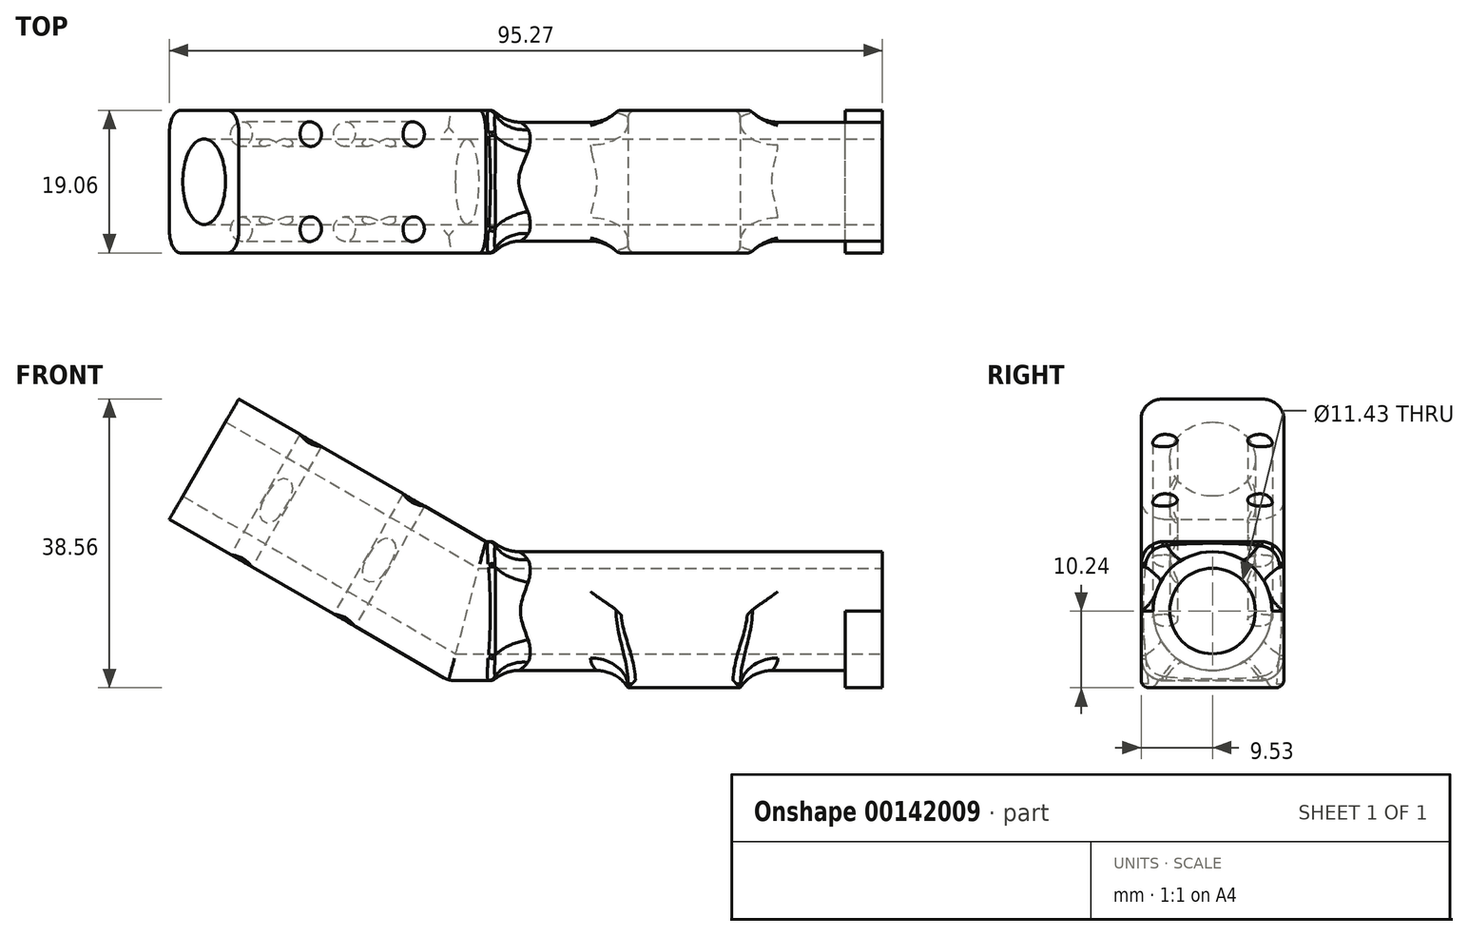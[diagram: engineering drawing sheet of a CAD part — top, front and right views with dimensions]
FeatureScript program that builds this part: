
annotation { "Feature Type Name" : "Feature", "Feature Type Description" : "" }
export const myFeature = defineFeature(function(context is Context, id is Id, definition is map)
    precondition{}
    {
        {
            var Q0;
            Q0=qCreatedBy(makeId("Front.planeOp"),FACE);
            var sketch = newSketch(context, id + "F0", { "sketchPlane" : qUnion([Q0])});
            skLineSegment(sketch, "E0.bottom", {"start": v(4.97, 9.27) * mm, "end": v(57.97, 9.27) * mm});
            skLineSegment(sketch, "E0.top", {"start": v(0, -9.27) * mm, "end": v(57.97, -9.27) * mm});
            skLineSegment(sketch, "E0.right", {"start": v(57.97, 9.27) * mm, "end": v(57.97, -9.27) * mm});
            skLineSegment(sketch, "E1", {"start": v(0, 0) * mm, "end": v(57.97, 0) * mm, "construction": true});
            skLineSegment(sketch, "E2", {"start": v(4.97, 9.27) * mm, "end": v(-28.03, 28.32) * mm});
            skLineSegment(sketch, "E3", {"start": v(-37.3, 12.26) * mm, "end": v(-28.03, 28.32) * mm});
            skPoint(sketch, "E4.orphan", {"position": v(0, 13.5) * mm});
            skLineSegment(sketch, "E5", {"start": v(-37.3, 12.26) * mm, "end": v(0, -9.27) * mm});
            skSolve(sketch);
        }
        {
            var Q0;
            Q0=qSketchRegion(id+"F0",true);
            extrude(context, id + "F1", {"entities" : qUnion([Q0]), "depth" : 9.52 * mm, "hasSecondDirection" : true, "secondDirectionOppositeDirection" : true, "secondDirectionDepth" : 9.52 * mm});
        }
        {
            var Q0;
            Q0=makeQuery(id+"F1.opExtrude","SWEPT_FACE",FACE,{"disambiguationData":[OSD([sQuery(id+"F0.wireOp",EDGE,"E5")])]});
            var sketch = newSketch(context, id + "F2", { "sketchPlane" : qUnion([Q0])});
            skLineSegment(sketch, "E6.bottom", {"start": v(-38.43, -9.53) * mm, "end": v(-0.33, -9.53) * mm});
            skLineSegment(sketch, "E6.top", {"start": v(-38.43, 9.53) * mm, "end": v(-0.33, 9.53) * mm});
            skLineSegment(sketch, "E6.left", {"start": v(-38.43, -9.53) * mm, "end": v(-38.43, 9.53) * mm});
            skLineSegment(sketch, "E6.right", {"start": v(-0.33, -9.52) * mm, "end": v(-0.33, 9.53) * mm});
            skLineSegment(sketch, "E7", {"start": v(-38.43, 0) * mm, "end": v(-0.33, 0) * mm, "construction": true});
            skLineSegment(sketch, "E8", {"start": v(-19.38, 9.53) * mm, "end": v(-19.38, -9.53) * mm, "construction": true});
            skLineSegment(sketch, "E9.bottom", {"start": v(-27.32, -6.35) * mm, "end": v(-11.45, -6.35) * mm, "construction": true});
            skLineSegment(sketch, "E9.top", {"start": v(-27.32, 6.35) * mm, "end": v(-11.45, 6.35) * mm, "construction": true});
            skLineSegment(sketch, "E9.left", {"start": v(-27.32, -6.35) * mm, "end": v(-27.32, 6.35) * mm, "construction": true});
            skLineSegment(sketch, "E9.right", {"start": v(-11.45, -6.35) * mm, "end": v(-11.45, 6.35) * mm, "construction": true});
            skPoint(sketch, "E9.middle", {"position": v(-19.38, 0) * mm});
            skSolve(sketch);
        }
        {
            var Q0;
            Q0=sQuery(id+"F2.wireOp",VERTEX,"E9.left.end");
            var Q1;
            Q1=sQuery(id+"F2.wireOp",VERTEX,"E9.left.start");
            var Q2;
            Q2=sQuery(id+"F2.wireOp",VERTEX,"E9.right.start");
            var Q3;
            Q3=sQuery(id+"F2.wireOp",VERTEX,"E9.top.end");
            var Q4;
            Q4=makeQuery(id+"F1.opExtrude","SWEPT_BODY",BODY,{"disambiguationData":[OSD([sQuery(id+"F0.wireOp",EDGE,"E0.bottom"),sQuery(id+"F0.wireOp",EDGE,"E0.top"),sQuery(id+"F0.wireOp",EDGE,"E0.right"),sQuery(id+"F0.wireOp",EDGE,"E2"),sQuery(id+"F0.wireOp",EDGE,"95kfVAff-3bN3-xnc1-YnyT-jtpb1TC5GENx"),sQuery(id+"F0.wireOp",EDGE,"E3")])]});
            hole(context, id + "F3", {"style" : HoleStyle.SIMPLE, "endStyle" : HoleEndStyle.THROUGH, "standardTappedOrClearance" : lookupTablePath({ "standard" : "ISO", "fit" : "Normal", "size" : "M3", "type" : "Clearance" }), "standardBlindInLast" : lookupTablePath({ "fit" : "Standard", "standard" : "ISO", "size" : "M3", "type" : "Clearance" }), "holeDiameter" : 3.3 * mm, "locations" : qUnion([Q0, Q1, Q2, Q3]), "scope" : qUnion([Q4]), "isTappedThrough" : true});
        }
        {
            var Q0;
            Q0=makeQuery(id+"F1.opExtrude","SWEPT_FACE",FACE,{"disambiguationData":[OSD([sQuery(id+"F0.wireOp",EDGE,"E3")])]});
            var sketch = newSketch(context, id + "F4", { "sketchPlane" : qUnion([Q0])});
            skLineSegment(sketch, "E10", {"start": v(0, 10.51) * mm, "end": v(0, -8.03) * mm, "construction": true});
            skCircle(sketch, "E11", {"center": v(0, 1.24) * mm, "radius": 5.72 * mm});
            skSolve(sketch);
        }
        {
            var Q0;
            Q0=qCreatedBy(makeId("Front.planeOp"),FACE);
            var sketch = newSketch(context, id + "F5", { "sketchPlane" : qUnion([Q0])});
            skLineSegment(sketch, "E12", {"start": v(-32.66, 20.3) * mm, "end": v(2.48, 0) * mm});
            skLineSegment(sketch, "E13", {"start": v(2.48, 0) * mm, "end": v(57.97, 0) * mm});
            skPoint(sketch, "E14", {"position": v(57.97, 0) * mm});
            skSolve(sketch);
        }
        {
            var Q0;
            Q0=qSketchRegion(id+"F4",true);
            var Q1;
            Q1=qConstructionFilter(qBodyType(qCreatedBy(id+"F5",EDGE),BodyType.WIRE),ConstructionObject.NO);
            sweep(context, id + "F6", {"operationType" : NewBodyOperationType.REMOVE, "profiles" : qUnion([Q0]), "path" : qUnion([Q1])});
        }
        {
            var Q0;
            Q0=makeQuery(id+"F1.opExtrude","SWEPT_FACE",FACE,{"disambiguationData":[OSD([sQuery(id+"F0.wireOp",EDGE,"E0.right")])]});
            var sketch = newSketch(context, id + "F7", { "sketchPlane" : qUnion([Q0])});
            skCircle(sketch, "E15", {"center": v(0, 0) * mm, "radius": 7.94 * mm});
            skLineSegment(sketch, "E16.0.0", {"start": v(9.53, -9.27) * mm, "end": v(9.53, 9.27) * mm});
            skLineSegment(sketch, "E16.0.1", {"start": v(9.52, 9.27) * mm, "end": v(-9.53, 9.27) * mm});
            skLineSegment(sketch, "E16.0.2", {"start": v(-9.53, 9.27) * mm, "end": v(-9.53, -9.27) * mm});
            skLineSegment(sketch, "E16.0.3", {"start": v(-9.53, -9.27) * mm, "end": v(9.52, -9.27) * mm});
            skSolve(sketch);
        }
        {
            var Q0;
            Q0=qSketchRegion(id+"F7",true);
            extrude(context, id + "F8", {"entities" : qUnion([Q0]), "operationType" : NewBodyOperationType.REMOVE, "oppositeDirection" : true, "depth" : 52 * mm});
        }
        {
            var Q0;
            Q0=makeQuery(id+"F1.opExtrude","SWEPT_FACE",FACE,{"disambiguationData":[OSD([sQuery(id+"F0.wireOp",EDGE,"E2")])]});
            var sketch = newSketch(context, id + "F9", { "sketchPlane" : qUnion([Q0])});
            skCircle(sketch, "E17.0", {"center": v(-27.32, -6.35) * mm, "radius": 1.65 * mm});
            skCircle(sketch, "E17.1", {"center": v(-27.32, 6.35) * mm, "radius": 1.65 * mm});
            skCircle(sketch, "E17.2", {"center": v(-11.45, -6.35) * mm, "radius": 1.65 * mm});
            skCircle(sketch, "E17.3", {"center": v(-11.45, 6.35) * mm, "radius": 1.65 * mm});
            skCircle(sketch, "E18", {"center": v(-27.32, -6.35) * mm, "radius": 3.18 * mm});
            skCircle(sketch, "E19", {"center": v(-27.32, 6.35) * mm, "radius": 3.18 * mm});
            skCircle(sketch, "E20", {"center": v(-11.45, 6.35) * mm, "radius": 3.18 * mm});
            skCircle(sketch, "E21", {"center": v(-11.45, -6.35) * mm, "radius": 3.18 * mm});
            skSolve(sketch);
        }
        {
            var Q0;
            Q0=makeQuery(id+"F1.opExtrude","CAP_EDGE",EDGE,{"disambiguationData":[OSD([sQuery(id+"F0.wireOp",EDGE,"E2")])],"isStart":true});
            var Q1;
            Q1=makeQuery(id+"F1.opExtrude","CAP_EDGE",EDGE,{"disambiguationData":[OSD([sQuery(id+"F0.wireOp",EDGE,"E2")])],"isStart":false});
            var Q2;
            Q2=makeQuery(id+"F1.opExtrude","CAP_EDGE",EDGE,{"disambiguationData":[OSD([sQuery(id+"F0.wireOp",EDGE,"E5")])],"isStart":false});
            var Q3;
            Q3=makeQuery(id+"F1.opExtrude","CAP_EDGE",EDGE,{"disambiguationData":[OSD([sQuery(id+"F0.wireOp",EDGE,"E5")])],"isStart":true});
            var Q4;
            Q4=makeQuery(id+"F1.opExtrude","CAP_EDGE",EDGE,{"disambiguationData":[OSD([sQuery(id+"F0.wireOp",EDGE,"E0.top")])],"isStart":false});
            var Q5;
            Q5=makeQuery(id+"F1.opExtrude","CAP_EDGE",EDGE,{"disambiguationData":[OSD([sQuery(id+"F0.wireOp",EDGE,"E0.top")])],"isStart":true});
            var Q6;
            {var subQ0=sQuery(id+"F0.wireOp",EDGE,"E2");var subQ1=sQuery(id+"F0.wireOp",EDGE,"E0.bottom");Q6=makeQuery(id+"FvCCCtX8j9DAQVm_1.opFillet","BLEND_EDGE",EDGE,{"blendedFrom":[makeQuery(id+"F1.opExtrude","SWEPT_EDGE",EDGE,{"disambiguationData":[OSD([subQ1,subQ0])]}),makeQuery(id+"F1.opExtrude","CAP_FACE",FACE,{"disambiguationData":[OSD([subQ1,sQuery(id+"F0.wireOp",EDGE,"E0.top"),sQuery(id+"F0.wireOp",EDGE,"E0.right"),subQ0,sQuery(id+"F0.wireOp",EDGE,"E3"),sQuery(id+"F0.wireOp",EDGE,"E5")])],"isStart":false})],"blendedInto":[makeQuery(id+"F1.opExtrude","CAP_FACE",FACE,{"disambiguationData":[OSD([subQ1,sQuery(id+"F0.wireOp",EDGE,"E0.top"),sQuery(id+"F0.wireOp",EDGE,"E0.right"),subQ0,sQuery(id+"F0.wireOp",EDGE,"E3"),sQuery(id+"F0.wireOp",EDGE,"E5")])],"isStart":false})]});}
            var Q7;
            Q7=makeQuery(id+"F1.opExtrude","CAP_EDGE",EDGE,{"disambiguationData":[OSD([sQuery(id+"F0.wireOp",EDGE,"E0.bottom")])],"isStart":false});
            var Q8;
            {var subQ0=sQuery(id+"F0.wireOp",EDGE,"E2");var subQ1=sQuery(id+"F0.wireOp",EDGE,"E0.bottom");Q8=makeQuery(id+"FvCCCtX8j9DAQVm_1.opFillet","BLEND_EDGE",EDGE,{"blendedFrom":[makeQuery(id+"F1.opExtrude","SWEPT_EDGE",EDGE,{"disambiguationData":[OSD([subQ1,subQ0])]}),makeQuery(id+"F1.opExtrude","CAP_FACE",FACE,{"disambiguationData":[OSD([subQ1,sQuery(id+"F0.wireOp",EDGE,"E0.top"),sQuery(id+"F0.wireOp",EDGE,"E0.right"),subQ0,sQuery(id+"F0.wireOp",EDGE,"E3"),sQuery(id+"F0.wireOp",EDGE,"E5")])],"isStart":true})],"blendedInto":[makeQuery(id+"F1.opExtrude","CAP_FACE",FACE,{"disambiguationData":[OSD([subQ1,sQuery(id+"F0.wireOp",EDGE,"E0.top"),sQuery(id+"F0.wireOp",EDGE,"E0.right"),subQ0,sQuery(id+"F0.wireOp",EDGE,"E3"),sQuery(id+"F0.wireOp",EDGE,"E5")])],"isStart":true})]});}
            var Q9;
            Q9=makeQuery(id+"F1.opExtrude","CAP_EDGE",EDGE,{"disambiguationData":[OSD([sQuery(id+"F0.wireOp",EDGE,"E0.bottom")])],"isStart":true});
            fillet(context, id + "F10", {"entities" : qUnion([Q0, Q1, Q2, Q3, Q4, Q5, Q6, Q7, Q8, Q9]), "radius" : 3 * mm, "allowEdgeOverflow" : false});
        }
        {
            var Q0;
            Q0=qCreatedBy(makeId("Front.planeOp"),FACE);
            var sketch = newSketch(context, id + "F11", { "sketchPlane" : qUnion([Q0])});
            skCircle(sketch, "E22", {"center": v(42.1, 0) * mm, "radius": 1.65 * mm});
            skSolve(sketch);
        }
        {
            var Q0;
            Q0=makeQuery(id+"F1.opExtrude","SWEPT_EDGE",EDGE,{"disambiguationData":[OSD([sQuery(id+"F0.wireOp",EDGE,"E0.top"),sQuery(id+"F0.wireOp",EDGE,"E5")])]});
            var Q1;
            Q1=makeQuery(id+"FvCCCtX8j9DAQVm_1.opFillet","BLEND_EDGE",EDGE,{"blendedFrom":[makeQuery(id+"F8.boolean.opBoolean","COPY",EDGE,{"derivedFrom":makeQuery(id+"F8.opExtrude","CAP_EDGE",EDGE,{"disambiguationData":[OSD([sQuery(id+"F7.wireOp",EDGE,"E15")])],"isStart":false})}),makeQuery(id+"F1.opExtrude","SWEPT_FACE",FACE,{"disambiguationData":[OSD([sQuery(id+"F0.wireOp",EDGE,"E0.top")])]})],"blendedInto":[makeQuery(id+"F1.opExtrude","SWEPT_FACE",FACE,{"disambiguationData":[OSD([sQuery(id+"F0.wireOp",EDGE,"E0.top")])]})]});
            fillet(context, id + "F12", {"entities" : qUnion([Q0, Q1]), "radius" : 2.54 * mm, "allowEdgeOverflow" : false});
        }
        {
            var Q0;
            Q0=qCreatedBy(makeId("Right.planeOp"),FACE);
            var Q1;
            Q1=makeQuery(id+"F1.opExtrude","SWEPT_FACE",FACE,{"disambiguationData":[OSD([sQuery(id+"F0.wireOp",EDGE,"E0.right")])]});
            cPlane(context, id + "F13", {"entities" : qUnion([Q0, Q1]), "cplaneType" : CPlaneType.MID_PLANE, "offset" : 25 * mm, "width" : 150 * mm, "height" : 150 * mm});
        }
        {
            var Q0;
            Q0=qCreatedBy(id+"F13.planeOp",FACE);
            var sketch = newSketch(context, id + "F14", { "sketchPlane" : qUnion([Q0])});
            skCircle(sketch, "E23", {"center": v(0, 0) * mm, "radius": 7.94 * mm, "construction": true});
            skArc(sketch, "E24", {"start": v(-5.72, 0) * mm, "mid": v(0, -5.72) * mm, "end": v(5.72, 0) * mm});
            skLineSegment(sketch, "E25.top", {"start": v(9.53, -10.24) * mm, "end": v(-9.53, -10.24) * mm});
            skLineSegment(sketch, "E25.left", {"start": v(9.53, 0) * mm, "end": v(9.53, -10.24) * mm});
            skLineSegment(sketch, "E25.right", {"start": v(-9.53, 0) * mm, "end": v(-9.53, -10.24) * mm});
            skLineSegment(sketch, "E26", {"start": v(-9.53, 0) * mm, "end": v(-5.72, 0) * mm});
            skLineSegment(sketch, "E27", {"start": v(5.72, 0) * mm, "end": v(9.53, 0) * mm});
            skPoint(sketch, "E25.bottom.end.orphan", {"position": v(-9.53, 10.24) * mm});
            skPoint(sketch, "E28.orphan", {"position": v(9.53, 10.24) * mm});
            skSolve(sketch);
        }
        {
            var Q0;
            Q0 = qSketchRegion(id + "F14", true);
            extrude(context, id + "F15", {"entities" : qUnion([Q0]), "operationType" : NewBodyOperationType.ADD, "depth" : 10 * mm, "hasSecondDirection" : true, "secondDirectionOppositeDirection" : true, "secondDirectionDepth" : 5 * mm});
        }
        {
            var Q0;
            Q0=makeQuery(id+"F8.boolean.opBoolean","COPY",FACE,{"derivedFrom":makeQuery(id+"F8.opExtrude","CAP_FACE",FACE,{"disambiguationData":[OSD([sQuery(id+"F7.wireOp",EDGE,"E15"),sQuery(id+"F7.wireOp",EDGE,"E16.0.0"),sQuery(id+"F7.wireOp",EDGE,"E16.0.1"),sQuery(id+"F7.wireOp",EDGE,"E16.0.2"),sQuery(id+"F7.wireOp",EDGE,"E16.0.3")])],"isStart":false})});
            var sketch = newSketch(context, id + "F16", { "sketchPlane" : qUnion([Q0])});
            skArc(sketch, "E29", {"start": v(7.94, 0) * mm, "mid": v(0, 7.94) * mm, "end": v(-7.94, 0) * mm});
            skPoint(sketch, "E30.firstSnap0", {"position": v(-8.65, 9.27) * mm});
            skLineSegment(sketch, "E30.bottom", {"start": v(-9.53, 9.27) * mm, "end": v(9.53, 9.27) * mm});
            skLineSegment(sketch, "E30.top", {"start": v(-9.52, 0) * mm, "end": v(-7.94, 0) * mm});
            skLineSegment(sketch, "E30.left", {"start": v(-9.53, 9.27) * mm, "end": v(-9.53, 0) * mm});
            skLineSegment(sketch, "E30.right", {"start": v(9.53, 9.27) * mm, "end": v(9.53, 0) * mm});
            skLineSegment(sketch, "E31.trimOffspring", {"start": v(7.94, 0) * mm, "end": v(9.53, 0) * mm});
            skSolve(sketch);
        }
        {
            var Q0;
            Q0=makeQuery(id+"F1.opExtrude","SWEPT_FACE",FACE,{"disambiguationData":[OSD([sQuery(id+"F0.wireOp",EDGE,"E0.right")])]});
            var sketch = newSketch(context, id + "F17", { "sketchPlane" : qUnion([Q0])});
            skArc(sketch, "E32", {"start": v(-7.94, 0) * mm, "mid": v(0, -7.94) * mm, "end": v(7.94, 0) * mm});
            skLineSegment(sketch, "E33.bottom", {"start": v(-9.53, -10.24) * mm, "end": v(9.53, -10.24) * mm});
            skLineSegment(sketch, "E33.top", {"start": v(-9.53, 0) * mm, "end": v(-7.94, 0) * mm});
            skLineSegment(sketch, "E33.left", {"start": v(-9.53, -10.24) * mm, "end": v(-9.53, 0) * mm});
            skLineSegment(sketch, "E33.right", {"start": v(9.53, -10.24) * mm, "end": v(9.52, 0) * mm});
            skLineSegment(sketch, "E34.trimOffspring", {"start": v(7.94, 0) * mm, "end": v(9.52, 0) * mm});
            skSolve(sketch);
        }
        {
            var Q0;
            Q0 = qSketchRegion(id + "F17", true);
            extrude(context, id + "F18", {"entities" : qUnion([Q0]), "operationType" : NewBodyOperationType.ADD, "oppositeDirection" : true, "depth" : 5 * mm});
        }
        {
            var Q0;
            Q0=makeQuery(id+"F8.boolean.opBoolean","COPY",EDGE,{"derivedFrom":makeQuery(id+"F8.opExtrude","CAP_EDGE",EDGE,{"disambiguationData":[OSD([sQuery(id+"F7.wireOp",EDGE,"E15")])],"isStart":false})});
            var Q1;
            Q1=makeQuery(id+"F15.boolean.opBoolean","INTERSECT",EDGE,{"derivedFrom":[makeQuery(id+"F8.boolean.opBoolean","COPY",FACE,{"derivedFrom":makeQuery(id+"F8.opExtrude","SWEPT_FACE",FACE,{"disambiguationData":[OSD([sQuery(id+"F7.wireOp",EDGE,"E15")])]})}),makeQuery(id+"F15.opExtrude","CAP_FACE",FACE,{"disambiguationData":[OSD([sQuery(id+"F14.wireOp",EDGE,"E24"),sQuery(id+"F14.wireOp",EDGE,"E25.top"),sQuery(id+"F14.wireOp",EDGE,"E25.left"),sQuery(id+"F14.wireOp",EDGE,"E25.right"),sQuery(id+"F14.wireOp",EDGE,"E26"),sQuery(id+"F14.wireOp",EDGE,"E27")])],"isStart":false})]});
            var Q2;
            Q2=makeQuery(id+"F15.boolean.opBoolean","INTERSECT",EDGE,{"derivedFrom":[makeQuery(id+"F8.boolean.opBoolean","COPY",FACE,{"derivedFrom":makeQuery(id+"F8.opExtrude","SWEPT_FACE",FACE,{"disambiguationData":[OSD([sQuery(id+"F7.wireOp",EDGE,"E15")])]})}),makeQuery(id+"F15.opExtrude","CAP_FACE",FACE,{"disambiguationData":[OSD([sQuery(id+"F14.wireOp",EDGE,"E24"),sQuery(id+"F14.wireOp",EDGE,"E25.top"),sQuery(id+"F14.wireOp",EDGE,"E25.left"),sQuery(id+"F14.wireOp",EDGE,"E25.right"),sQuery(id+"F14.wireOp",EDGE,"E26"),sQuery(id+"F14.wireOp",EDGE,"E27")])],"isStart":true})]});
            var Q3;
            Q3=makeQuery(id+"F15.boolean.opBoolean","INTERSECT",EDGE,{"derivedFrom":[makeQuery(id+"F8.boolean.opBoolean","COPY",FACE,{"derivedFrom":makeQuery(id+"F8.opExtrude","SWEPT_FACE",FACE,{"disambiguationData":[OSD([sQuery(id+"F7.wireOp",EDGE,"E15")])]})}),makeQuery(id+"F15.opExtrude","SWEPT_FACE",FACE,{"disambiguationData":[OSD([sQuery(id+"F14.wireOp",EDGE,"E26")])]})]});
            var Q4;
            Q4=makeQuery(id+"F15.boolean.opBoolean","INTERSECT",EDGE,{"derivedFrom":[makeQuery(id+"F8.boolean.opBoolean","COPY",FACE,{"derivedFrom":makeQuery(id+"F8.opExtrude","SWEPT_FACE",FACE,{"disambiguationData":[OSD([sQuery(id+"F7.wireOp",EDGE,"E15")])]})}),makeQuery(id+"F15.opExtrude","SWEPT_FACE",FACE,{"disambiguationData":[OSD([sQuery(id+"F14.wireOp",EDGE,"E27")])]})]});
            var Q5;
            Q5=makeQuery(id+"F18.opExtrude","SWEPT_EDGE",EDGE,{"disambiguationData":[OSD([sQuery(id+"F7.wireOp",EDGE,"E15"),sQuery(id+"F17.wireOp",EDGE,"E32"),sQuery(id+"F17.wireOp",EDGE,"E34.trimOffspring")])]});
            var Q6;
            Q6=makeQuery(id+"F18.opExtrude","SWEPT_EDGE",EDGE,{"disambiguationData":[OSD([sQuery(id+"F7.wireOp",EDGE,"E15"),sQuery(id+"F17.wireOp",EDGE,"E32"),sQuery(id+"F17.wireOp",EDGE,"E33.top")])]});
            var Q7;
            Q7=makeQuery(id+"F18.opExtrude","CAP_EDGE",EDGE,{"disambiguationData":[OSD([sQuery(id+"F17.wireOp",EDGE,"E32")])],"isStart":false});
            fillet(context, id + "F19", {"entities" : qUnion([Q0, Q1, Q2, Q3, Q4, Q5, Q6, Q7]), "radius" : 5 * mm, "tangentPropagation" : true, "allowEdgeOverflow" : false});
        }
        {
            var Q0;
            Q0=makeQuery(id+"F19.opFillet","BLEND_EDGE",EDGE,{"blendedFrom":[makeQuery(id+"F15.boolean.opBoolean","INTERSECT",EDGE,{"derivedFrom":[makeQuery(id+"F8.boolean.opBoolean","COPY",FACE,{"derivedFrom":makeQuery(id+"F8.opExtrude","SWEPT_FACE",FACE,{"disambiguationData":[OSD([sQuery(id+"F7.wireOp",EDGE,"E15")])]})}),makeQuery(id+"F15.opExtrude","SWEPT_FACE",FACE,{"disambiguationData":[OSD([sQuery(id+"F14.wireOp",EDGE,"E26")])]})]}),makeQuery(id+"F15.opExtrude","SWEPT_FACE",FACE,{"disambiguationData":[OSD([sQuery(id+"F14.wireOp",EDGE,"E25.right")])]})],"blendedInto":[makeQuery(id+"F15.opExtrude","SWEPT_FACE",FACE,{"disambiguationData":[OSD([sQuery(id+"F14.wireOp",EDGE,"E25.right")])]})]});
            var Q1;
            {var subQ0=sQuery(id+"F14.wireOp",EDGE,"E25.right");Q1=makeQuery(id+"F19.opFillet","BLEND_EDGE",EDGE,{"blendedFrom":[makeQuery(id+"F15.boolean.opBoolean","INTERSECT",EDGE,{"derivedFrom":[makeQuery(id+"F8.boolean.opBoolean","COPY",FACE,{"derivedFrom":makeQuery(id+"F8.opExtrude","SWEPT_FACE",FACE,{"disambiguationData":[OSD([sQuery(id+"F7.wireOp",EDGE,"E15")])]})}),makeQuery(id+"F15.opExtrude","CAP_FACE",FACE,{"disambiguationData":[OSD([sQuery(id+"F14.wireOp",EDGE,"E24"),sQuery(id+"F14.wireOp",EDGE,"E25.top"),sQuery(id+"F14.wireOp",EDGE,"E25.left"),subQ0,sQuery(id+"F14.wireOp",EDGE,"E26"),sQuery(id+"F14.wireOp",EDGE,"E27")])],"isStart":true})]}),makeQuery(id+"F15.opExtrude","SWEPT_FACE",FACE,{"disambiguationData":[OSD([subQ0])]})],"blendedInto":[makeQuery(id+"F15.opExtrude","SWEPT_FACE",FACE,{"disambiguationData":[OSD([subQ0])]})]});}
            var Q2;
            {var subQ0=sQuery(id+"F14.wireOp",EDGE,"E25.right");Q2=makeQuery(id+"F19.opFillet","BLEND_EDGE",EDGE,{"blendedFrom":[makeQuery(id+"F15.boolean.opBoolean","INTERSECT",EDGE,{"derivedFrom":[makeQuery(id+"F8.boolean.opBoolean","COPY",FACE,{"derivedFrom":makeQuery(id+"F8.opExtrude","SWEPT_FACE",FACE,{"disambiguationData":[OSD([sQuery(id+"F7.wireOp",EDGE,"E15")])]})}),makeQuery(id+"F15.opExtrude","CAP_FACE",FACE,{"disambiguationData":[OSD([sQuery(id+"F14.wireOp",EDGE,"E24"),sQuery(id+"F14.wireOp",EDGE,"E25.top"),sQuery(id+"F14.wireOp",EDGE,"E25.left"),subQ0,sQuery(id+"F14.wireOp",EDGE,"E26"),sQuery(id+"F14.wireOp",EDGE,"E27")])],"isStart":false})]}),makeQuery(id+"F15.opExtrude","SWEPT_FACE",FACE,{"disambiguationData":[OSD([subQ0])]})],"blendedInto":[makeQuery(id+"F15.opExtrude","SWEPT_FACE",FACE,{"disambiguationData":[OSD([subQ0])]})]});}
            var Q3;
            Q3=makeQuery(id+"F19.opFillet","BLEND_EDGE",EDGE,{"blendedFrom":[makeQuery(id+"F18.opExtrude","SWEPT_EDGE",EDGE,{"disambiguationData":[OSD([sQuery(id+"F7.wireOp",EDGE,"E15"),sQuery(id+"F17.wireOp",EDGE,"E32"),sQuery(id+"F17.wireOp",EDGE,"E33.top")])]}),makeQuery(id+"F18.opExtrude","SWEPT_FACE",FACE,{"disambiguationData":[OSD([sQuery(id+"F17.wireOp",EDGE,"E33.left")])]})],"blendedInto":[makeQuery(id+"F18.opExtrude","SWEPT_FACE",FACE,{"disambiguationData":[OSD([sQuery(id+"F17.wireOp",EDGE,"E33.left")])]})]});
            var Q4;
            Q4=makeQuery(id+"F19.opFillet","BLEND_EDGE",EDGE,{"blendedFrom":[makeQuery(id+"F18.opExtrude","CAP_EDGE",EDGE,{"disambiguationData":[OSD([sQuery(id+"F17.wireOp",EDGE,"E32")])],"isStart":false}),makeQuery(id+"F18.opExtrude","SWEPT_FACE",FACE,{"disambiguationData":[OSD([sQuery(id+"F17.wireOp",EDGE,"E33.left")])]})],"blendedInto":[makeQuery(id+"F18.opExtrude","SWEPT_FACE",FACE,{"disambiguationData":[OSD([sQuery(id+"F17.wireOp",EDGE,"E33.left")])]})]});
            var Q5;
            Q5=makeQuery(id+"F19.opFillet","BLEND_EDGE",EDGE,{"blendedFrom":[makeQuery(id+"F8.boolean.opBoolean","COPY",EDGE,{"derivedFrom":makeQuery(id+"F8.opExtrude","CAP_EDGE",EDGE,{"disambiguationData":[OSD([sQuery(id+"F7.wireOp",EDGE,"E15")])],"isStart":false})}),makeQuery(id+"F1.opExtrude","CAP_FACE",FACE,{"disambiguationData":[OSD([sQuery(id+"F0.wireOp",EDGE,"E0.bottom"),sQuery(id+"F0.wireOp",EDGE,"E0.top"),sQuery(id+"F0.wireOp",EDGE,"E0.right"),sQuery(id+"F0.wireOp",EDGE,"E2"),sQuery(id+"F0.wireOp",EDGE,"E3"),sQuery(id+"F0.wireOp",EDGE,"E5")])],"isStart":false})],"blendedInto":[makeQuery(id+"F1.opExtrude","CAP_FACE",FACE,{"disambiguationData":[OSD([sQuery(id+"F0.wireOp",EDGE,"E0.bottom"),sQuery(id+"F0.wireOp",EDGE,"E0.top"),sQuery(id+"F0.wireOp",EDGE,"E0.right"),sQuery(id+"F0.wireOp",EDGE,"E2"),sQuery(id+"F0.wireOp",EDGE,"E3"),sQuery(id+"F0.wireOp",EDGE,"E5")])],"isStart":false})]});
            var Q6;
            {var subQ0=sQuery(id+"F0.wireOp",EDGE,"E0.bottom");Q6=makeQuery(id+"F19.opFillet","BLEND_EDGE",EDGE,{"blendedFrom":[makeQuery(id+"F8.boolean.opBoolean","COPY",EDGE,{"derivedFrom":makeQuery(id+"F8.opExtrude","CAP_EDGE",EDGE,{"disambiguationData":[OSD([sQuery(id+"F7.wireOp",EDGE,"E15")])],"isStart":false})}),makeQuery(id+"F10.opFillet","BLEND_FACE",FACE,{"disambiguationData":[OSD([subQ0]),TDD([makeQuery(id+"F1.opExtrude","CAP_EDGE",EDGE,{"disambiguationData":[OSD([subQ0])],"isStart":false})])]})],"blendedInto":[makeQuery(id+"F10.opFillet","BLEND_FACE",FACE,{"disambiguationData":[OSD([subQ0]),TDD([makeQuery(id+"F1.opExtrude","CAP_EDGE",EDGE,{"disambiguationData":[OSD([subQ0])],"isStart":false})])]})]});}
            var Q7;
            Q7=makeQuery(id+"F19.opFillet","BLEND_EDGE",EDGE,{"blendedFrom":[makeQuery(id+"F8.boolean.opBoolean","COPY",EDGE,{"derivedFrom":makeQuery(id+"F8.opExtrude","CAP_EDGE",EDGE,{"disambiguationData":[OSD([sQuery(id+"F7.wireOp",EDGE,"E15")])],"isStart":false})}),makeQuery(id+"F1.opExtrude","SWEPT_FACE",FACE,{"disambiguationData":[OSD([sQuery(id+"F0.wireOp",EDGE,"E0.bottom")])]})],"blendedInto":[makeQuery(id+"F1.opExtrude","SWEPT_FACE",FACE,{"disambiguationData":[OSD([sQuery(id+"F0.wireOp",EDGE,"E0.bottom")])]})]});
            var Q8;
            Q8=makeQuery(id+"F19.opFillet","BLEND_EDGE",EDGE,{"blendedFrom":[makeQuery(id+"F15.boolean.opBoolean","INTERSECT",EDGE,{"derivedFrom":[makeQuery(id+"F8.boolean.opBoolean","COPY",FACE,{"derivedFrom":makeQuery(id+"F8.opExtrude","SWEPT_FACE",FACE,{"disambiguationData":[OSD([sQuery(id+"F7.wireOp",EDGE,"E15")])]})}),makeQuery(id+"F15.opExtrude","SWEPT_FACE",FACE,{"disambiguationData":[OSD([sQuery(id+"F14.wireOp",EDGE,"E27")])]})]}),makeQuery(id+"F15.opExtrude","SWEPT_FACE",FACE,{"disambiguationData":[OSD([sQuery(id+"F14.wireOp",EDGE,"E25.left")])]})],"blendedInto":[makeQuery(id+"F15.opExtrude","SWEPT_FACE",FACE,{"disambiguationData":[OSD([sQuery(id+"F14.wireOp",EDGE,"E25.left")])]})]});
            var Q9;
            {var subQ0=sQuery(id+"F14.wireOp",EDGE,"E25.left");Q9=makeQuery(id+"F19.opFillet","BLEND_EDGE",EDGE,{"blendedFrom":[makeQuery(id+"F15.boolean.opBoolean","INTERSECT",EDGE,{"derivedFrom":[makeQuery(id+"F8.boolean.opBoolean","COPY",FACE,{"derivedFrom":makeQuery(id+"F8.opExtrude","SWEPT_FACE",FACE,{"disambiguationData":[OSD([sQuery(id+"F7.wireOp",EDGE,"E15")])]})}),makeQuery(id+"F15.opExtrude","CAP_FACE",FACE,{"disambiguationData":[OSD([sQuery(id+"F14.wireOp",EDGE,"E24"),sQuery(id+"F14.wireOp",EDGE,"E25.top"),subQ0,sQuery(id+"F14.wireOp",EDGE,"E25.right"),sQuery(id+"F14.wireOp",EDGE,"E26"),sQuery(id+"F14.wireOp",EDGE,"E27")])],"isStart":true})]}),makeQuery(id+"F15.opExtrude","SWEPT_FACE",FACE,{"disambiguationData":[OSD([subQ0])]})],"blendedInto":[makeQuery(id+"F15.opExtrude","SWEPT_FACE",FACE,{"disambiguationData":[OSD([subQ0])]})]});}
            var Q10;
            {var subQ0=sQuery(id+"F14.wireOp",EDGE,"E25.left");Q10=makeQuery(id+"F19.opFillet","BLEND_EDGE",EDGE,{"blendedFrom":[makeQuery(id+"F15.boolean.opBoolean","INTERSECT",EDGE,{"derivedFrom":[makeQuery(id+"F8.boolean.opBoolean","COPY",FACE,{"derivedFrom":makeQuery(id+"F8.opExtrude","SWEPT_FACE",FACE,{"disambiguationData":[OSD([sQuery(id+"F7.wireOp",EDGE,"E15")])]})}),makeQuery(id+"F15.opExtrude","CAP_FACE",FACE,{"disambiguationData":[OSD([sQuery(id+"F14.wireOp",EDGE,"E24"),sQuery(id+"F14.wireOp",EDGE,"E25.top"),subQ0,sQuery(id+"F14.wireOp",EDGE,"E25.right"),sQuery(id+"F14.wireOp",EDGE,"E26"),sQuery(id+"F14.wireOp",EDGE,"E27")])],"isStart":false})]}),makeQuery(id+"F15.opExtrude","SWEPT_FACE",FACE,{"disambiguationData":[OSD([subQ0])]})],"blendedInto":[makeQuery(id+"F15.opExtrude","SWEPT_FACE",FACE,{"disambiguationData":[OSD([subQ0])]})]});}
            var Q11;
            Q11=makeQuery(id+"F19.opFillet","BLEND_EDGE",EDGE,{"blendedFrom":[makeQuery(id+"F18.opExtrude","SWEPT_EDGE",EDGE,{"disambiguationData":[OSD([sQuery(id+"F7.wireOp",EDGE,"E15"),sQuery(id+"F17.wireOp",EDGE,"E32"),sQuery(id+"F17.wireOp",EDGE,"E34.trimOffspring")])]}),makeQuery(id+"F18.opExtrude","SWEPT_FACE",FACE,{"disambiguationData":[OSD([sQuery(id+"F17.wireOp",EDGE,"E33.right")])]})],"blendedInto":[makeQuery(id+"F18.opExtrude","SWEPT_FACE",FACE,{"disambiguationData":[OSD([sQuery(id+"F17.wireOp",EDGE,"E33.right")])]})]});
            var Q12;
            Q12=makeQuery(id+"F19.opFillet","BLEND_EDGE",EDGE,{"blendedFrom":[makeQuery(id+"F18.opExtrude","CAP_EDGE",EDGE,{"disambiguationData":[OSD([sQuery(id+"F17.wireOp",EDGE,"E32")])],"isStart":false}),makeQuery(id+"F18.opExtrude","SWEPT_FACE",FACE,{"disambiguationData":[OSD([sQuery(id+"F17.wireOp",EDGE,"E33.right")])]})],"blendedInto":[makeQuery(id+"F18.opExtrude","SWEPT_FACE",FACE,{"disambiguationData":[OSD([sQuery(id+"F17.wireOp",EDGE,"E33.right")])]})]});
            var Q13;
            Q13=makeQuery(id+"F15.opExtrude","SWEPT_EDGE",EDGE,{"disambiguationData":[OSD([sQuery(id+"F14.wireOp",EDGE,"E25.top"),sQuery(id+"F14.wireOp",EDGE,"E25.left")])]});
            var Q14;
            Q14=makeQuery(id+"F18.opExtrude","SWEPT_EDGE",EDGE,{"disambiguationData":[OSD([sQuery(id+"F17.wireOp",EDGE,"E33.bottom"),sQuery(id+"F17.wireOp",EDGE,"E33.right")])]});
            var Q15;
            Q15=makeQuery(id+"F15.opExtrude","SWEPT_EDGE",EDGE,{"disambiguationData":[OSD([sQuery(id+"F14.wireOp",EDGE,"E25.top"),sQuery(id+"F14.wireOp",EDGE,"E25.right")])]});
            var Q16;
            Q16=makeQuery(id+"F18.opExtrude","SWEPT_EDGE",EDGE,{"disambiguationData":[OSD([sQuery(id+"F17.wireOp",EDGE,"E33.bottom"),sQuery(id+"F17.wireOp",EDGE,"E33.left")])]});
            fillet(context, id + "F20", {"entities" : qUnion([Q0, Q1, Q2, Q3, Q4, Q5, Q6, Q7, Q8, Q9, Q10, Q11, Q12, Q13, Q14, Q15, Q16]), "radius" : 1 * mm, "tangentPropagation" : true, "allowEdgeOverflow" : false});
        }
    });
